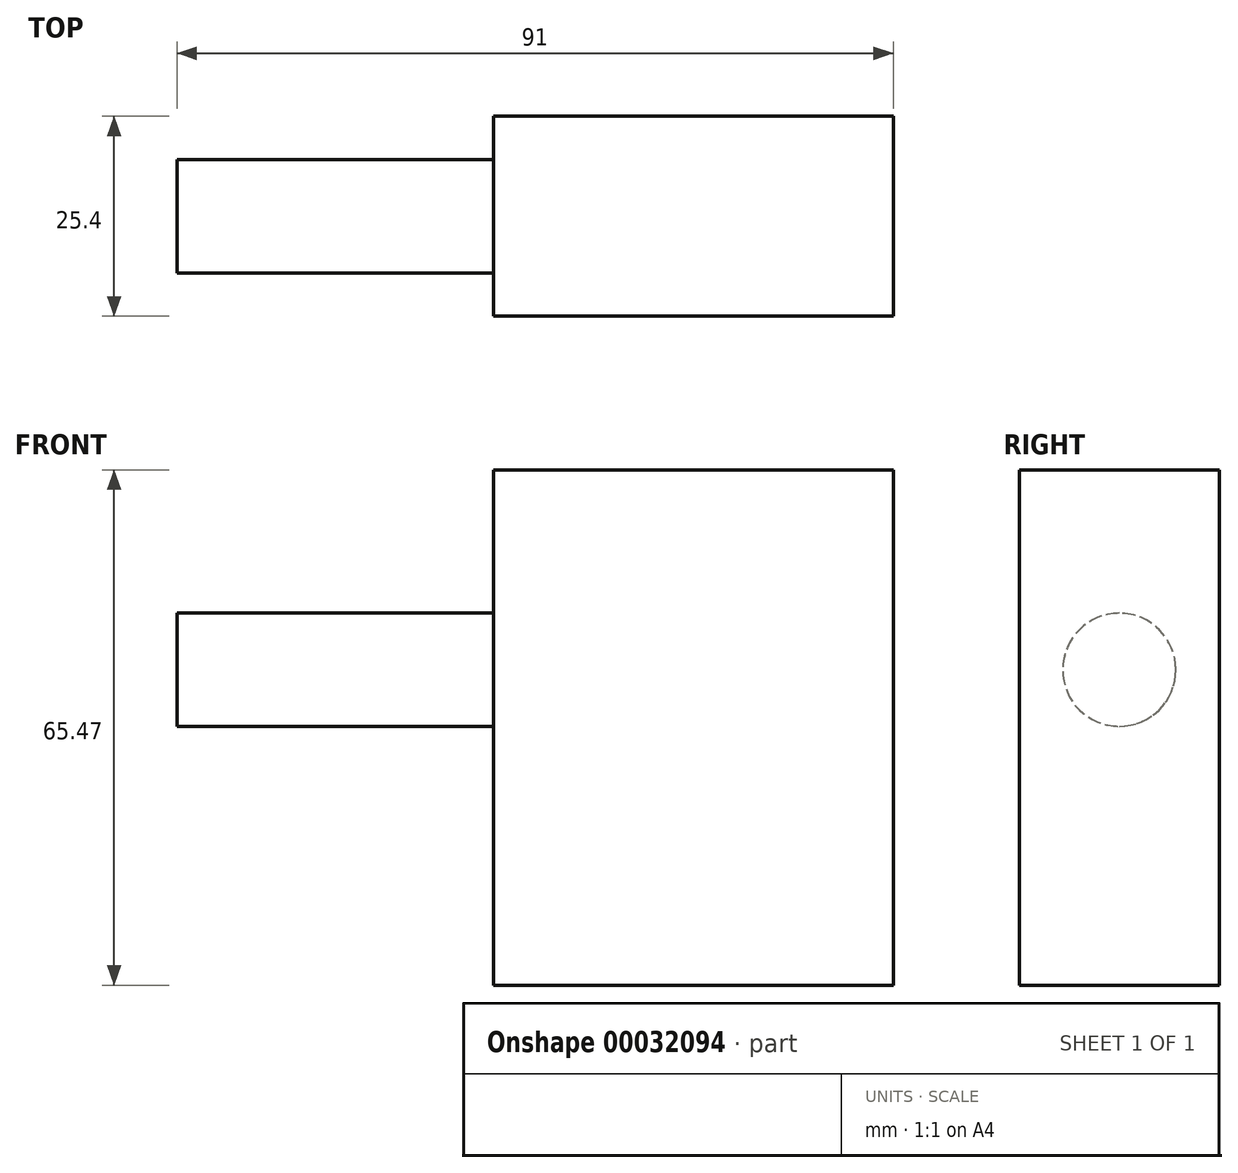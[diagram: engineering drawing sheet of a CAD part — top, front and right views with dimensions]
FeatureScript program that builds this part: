
annotation { "Feature Type Name" : "Feature", "Feature Type Description" : "" }
export const myFeature = defineFeature(function(context is Context, id is Id, definition is map)
    precondition{}
    {
        {
            var Q0;
            Q0=qCreatedBy(makeId("Top.planeOp"),FACE);
            var sketch = newSketch(context, id + "F0", { "sketchPlane" : qUnion([Q0])});
            skLineSegment(sketch, "E0.bottom", {"start": v(0, 0) * mm, "end": v(50.8, 0) * mm});
            skLineSegment(sketch, "E0.top", {"start": v(0, 25.4) * mm, "end": v(50.8, 25.4) * mm});
            skLineSegment(sketch, "E0.left", {"start": v(0, 0) * mm, "end": v(0, 25.4) * mm});
            skLineSegment(sketch, "E0.right", {"start": v(50.8, 0) * mm, "end": v(50.8, 25.4) * mm});
            skSolve(sketch);
        }
        {
            var Q0;
            Q0=makeQuery(id+"F0.imprint","IMPRINT",FACE,{"disambiguationData":[TD([[makeQuery(id+"F0.imprint","IMPRINT",EDGE,{"derivedFrom":sQuery(id+"F0.wireOp",EDGE,"E0.bottom")}),1.0]])]});
            extrude(context, id + "F1", {"entities" : qUnion([Q0]), "depth" : 65.47 * mm});
        }
        {
            var Q0;
            Q0=makeQuery(id+"F1.opExtrude","SWEPT_FACE",FACE,{"disambiguationData":[OSD([sQuery(id+"F0.wireOp",EDGE,"E0.right")])]});
            var sketch = newSketch(context, id + "F2", { "sketchPlane" : qUnion([Q0])});
            skCircle(sketch, "E1", {"center": v(12.7, 40.07) * mm, "radius": 7.19 * mm});
            skSolve(sketch);
        }
        {
            var Q0;
            Q0 = qSketchRegion(id + "F2", true);
            extrude(context, id + "F3", {"entities" : qUnion([Q0]), "operationType" : NewBodyOperationType.ADD, "oppositeDirection" : true, "depth" : 91 * mm});
        }
    });
